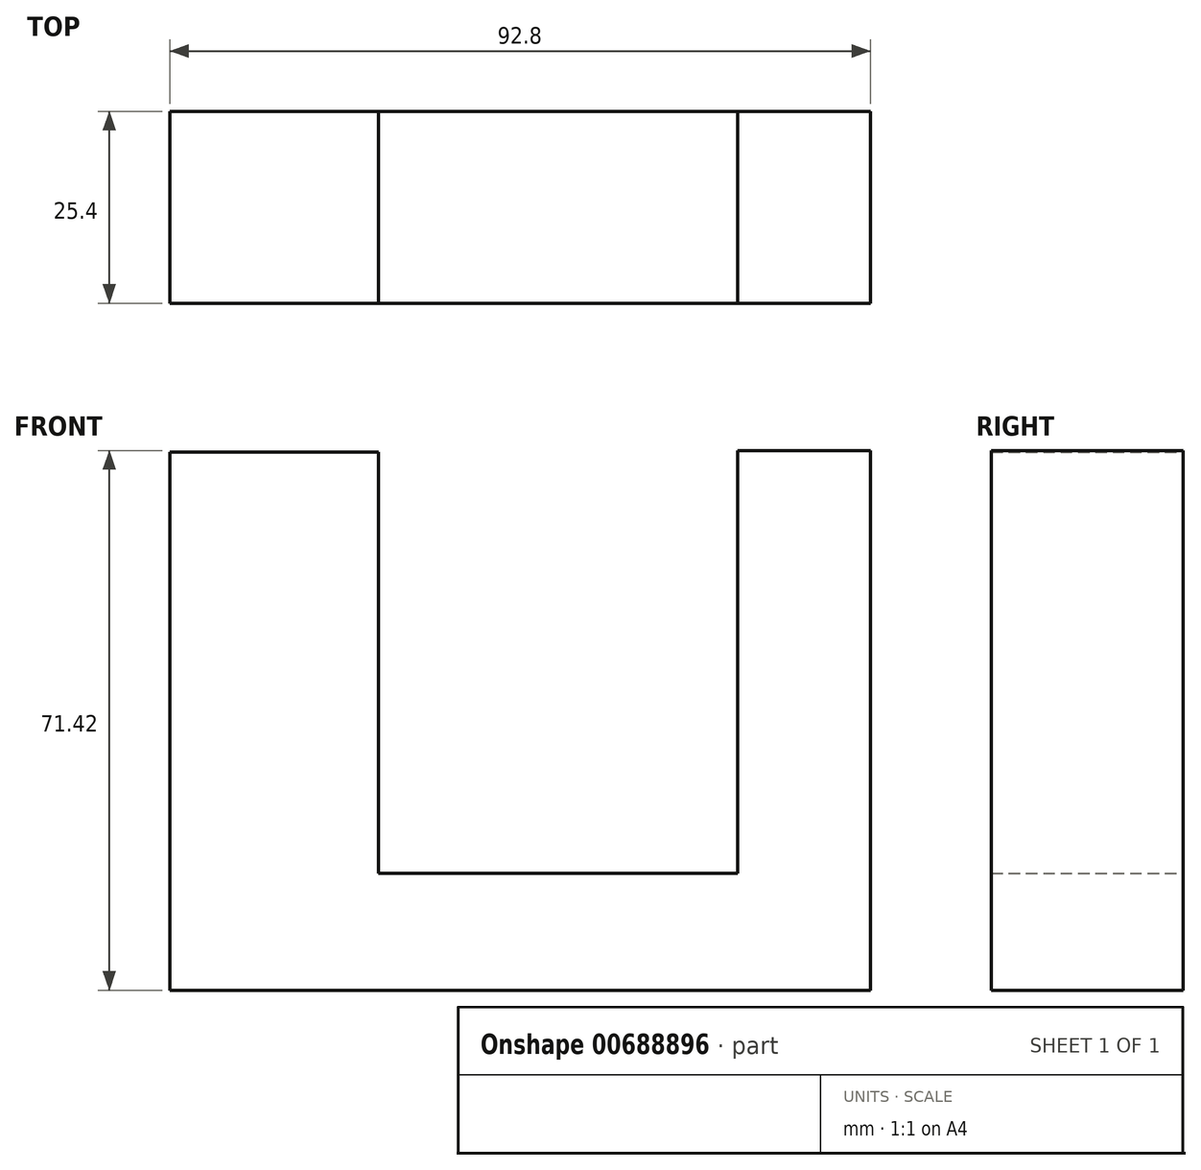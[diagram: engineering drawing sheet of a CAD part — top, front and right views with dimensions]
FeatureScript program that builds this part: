
annotation { "Feature Type Name" : "Feature", "Feature Type Description" : "" }
export const myFeature = defineFeature(function(context is Context, id is Id, definition is map)
    precondition{}
    {
        {
            var Q0;
            Q0=qCreatedBy(makeId("Front.planeOp"),FACE);
            var sketch = newSketch(context, id + "F0", { "sketchPlane" : qUnion([Q0])});
            skLineSegment(sketch, "E0", {"start": v(-53.56, 42.87) * mm, "end": v(-53.56, -28.36) * mm});
            skLineSegment(sketch, "E1", {"start": v(39.24, -28.36) * mm, "end": v(-53.56, -28.36) * mm});
            skLineSegment(sketch, "E2", {"start": v(39.24, -28.36) * mm, "end": v(39.24, 43.06) * mm});
            skLineSegment(sketch, "E3", {"start": v(39.24, 43.06) * mm, "end": v(21.67, 43.06) * mm});
            skLineSegment(sketch, "E4", {"start": v(21.67, 43.06) * mm, "end": v(21.67, -12.89) * mm});
            skLineSegment(sketch, "E5", {"start": v(21.67, -12.89) * mm, "end": v(-25.87, -12.89) * mm});
            skLineSegment(sketch, "E6", {"start": v(-25.87, -12.89) * mm, "end": v(-25.87, 42.87) * mm});
            skLineSegment(sketch, "E7", {"start": v(-25.87, 42.87) * mm, "end": v(-53.56, 42.87) * mm});
            skSolve(sketch);
        }
        {
            var Q0;
            Q0 = qSketchRegion(id + "F0", true);
            extrude(context, id + "F1", {"entities" : qUnion([Q0]), "depth" : 25.4 * mm, "offsetDistance" : 25.4 * mm});
        }
    });
